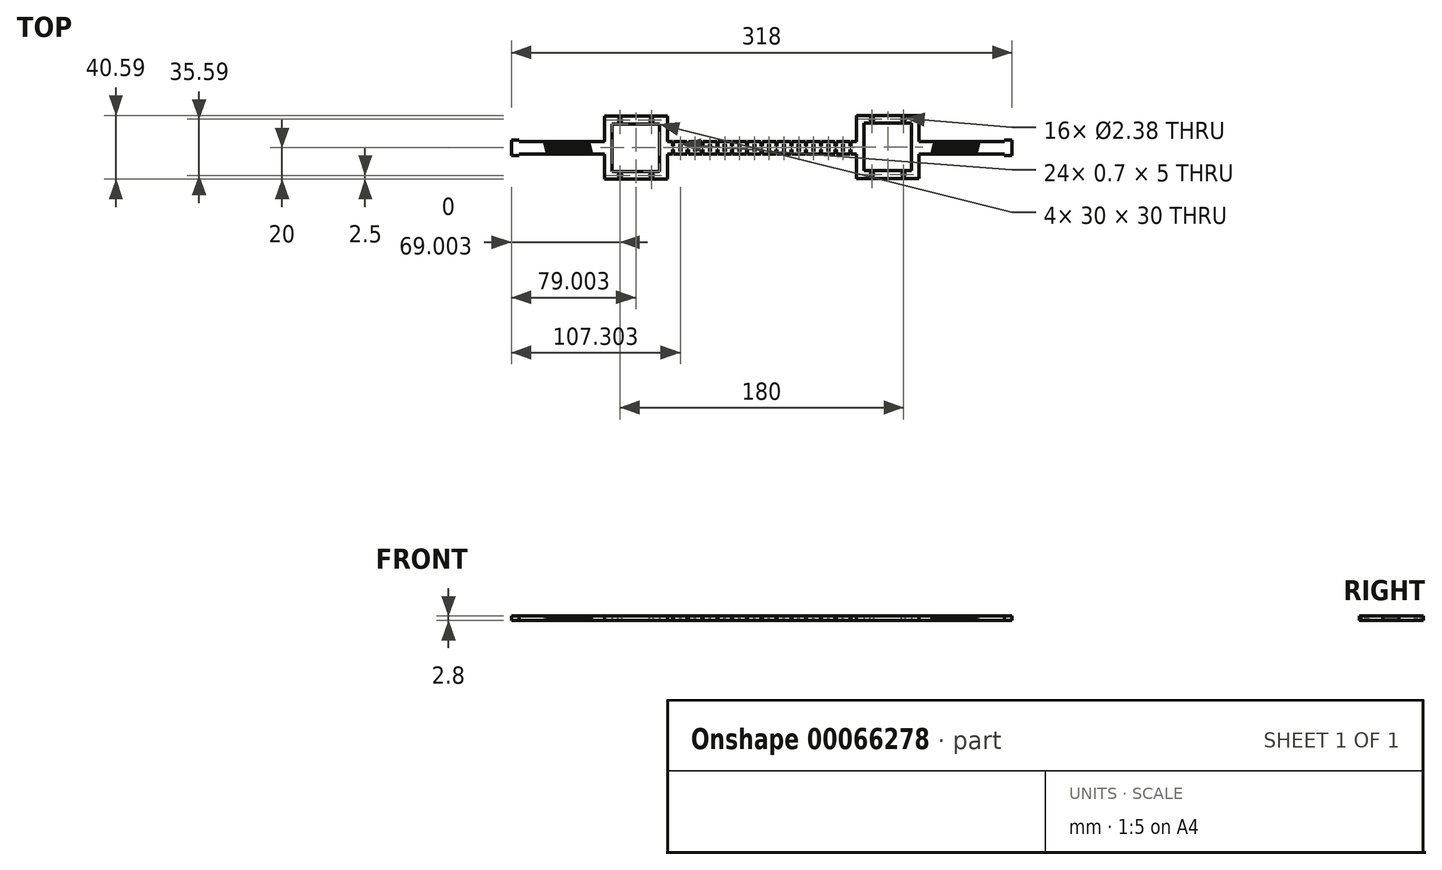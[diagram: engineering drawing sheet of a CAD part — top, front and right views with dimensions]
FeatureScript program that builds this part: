
annotation { "Feature Type Name" : "Feature", "Feature Type Description" : "" }
export const myFeature = defineFeature(function(context is Context, id is Id, definition is map)
    precondition{}
    {
        {
            var Q0;
            Q0=qCreatedBy(makeId("Top.planeOp"),FACE);
            var sketch = newSketch(context, id + "F0", { "sketchPlane" : qUnion([Q0])});
            skLineSegment(sketch, "E0.bottom", {"start": v(-118.62, 8) * mm, "end": v(-64.62, 8) * mm});
            skLineSegment(sketch, "E0.top", {"start": v(-118.62, 0) * mm, "end": v(-64.62, 0) * mm});
            skLineSegment(sketch, "E1.bottom", {"start": v(-64.62, 24) * mm, "end": v(-24.62, 24) * mm});
            skLineSegment(sketch, "E1.top", {"start": v(-64.62, -16) * mm, "end": v(-24.62, -16) * mm});
            skLineSegment(sketch, "E1.left", {"start": v(-64.62, 24) * mm, "end": v(-64.62, 8) * mm});
            skLineSegment(sketch, "E1.right", {"start": v(-24.62, 24) * mm, "end": v(-24.62, 8) * mm});
            skLineSegment(sketch, "E2.0", {"start": v(-59.62, 19) * mm, "end": v(-29.62, 19) * mm});
            skLineSegment(sketch, "E2.1", {"start": v(-59.62, 19) * mm, "end": v(-59.62, -11) * mm});
            skLineSegment(sketch, "E2.2", {"start": v(-59.62, -11) * mm, "end": v(-29.62, -11) * mm});
            skLineSegment(sketch, "E2.3", {"start": v(-29.62, 19) * mm, "end": v(-29.62, -11) * mm});
            skLineSegment(sketch, "E3.bottom", {"start": v(95.38, 24.6) * mm, "end": v(135.38, 24.6) * mm});
            skLineSegment(sketch, "E3.top", {"start": v(95.38, -15.4) * mm, "end": v(135.38, -15.4) * mm});
            skLineSegment(sketch, "E3.left", {"start": v(95.38, 24.6) * mm, "end": v(95.38, 8) * mm});
            skLineSegment(sketch, "E3.right", {"start": v(135.38, 24.6) * mm, "end": v(135.38, 8) * mm});
            skLineSegment(sketch, "E4.0", {"start": v(100.38, 19.6) * mm, "end": v(130.38, 19.6) * mm});
            skLineSegment(sketch, "E4.1", {"start": v(100.38, 19.6) * mm, "end": v(100.38, -10.4) * mm});
            skLineSegment(sketch, "E4.2", {"start": v(100.38, -10.4) * mm, "end": v(130.38, -10.4) * mm});
            skLineSegment(sketch, "E4.3", {"start": v(130.38, 19.6) * mm, "end": v(130.38, -10.4) * mm});
            skLineSegment(sketch, "E5.trimOffspring", {"start": v(-24.62, 8) * mm, "end": v(95.38, 8) * mm});
            skLineSegment(sketch, "E6.trimOffspring", {"start": v(-24.62, 0) * mm, "end": v(95.38, 0) * mm});
            skLineSegment(sketch, "E7.trimOffspring", {"start": v(-24.62, 0) * mm, "end": v(-24.62, -16) * mm});
            skLineSegment(sketch, "E8.trimOffspring", {"start": v(-64.62, 0) * mm, "end": v(-64.62, -16) * mm});
            skLineSegment(sketch, "E9.trimOffspring", {"start": v(135.38, 8) * mm, "end": v(189.38, 8) * mm});
            skLineSegment(sketch, "E10.trimOffspring", {"start": v(135.38, 0) * mm, "end": v(189.38, 0) * mm});
            skLineSegment(sketch, "E11.trimOffspring", {"start": v(95.38, 0) * mm, "end": v(95.38, -15.4) * mm});
            skLineSegment(sketch, "E12.trimOffspring", {"start": v(135.38, 0) * mm, "end": v(135.38, -15.4) * mm});
            skLineSegment(sketch, "E13.bottom", {"start": v(-123.62, 9) * mm, "end": v(-118.62, 9) * mm});
            skLineSegment(sketch, "E13.top", {"start": v(-123.62, -1) * mm, "end": v(-118.62, -1) * mm});
            skLineSegment(sketch, "E13.left", {"start": v(-123.62, 9) * mm, "end": v(-123.62, -1) * mm});
            skLineSegment(sketch, "E13.right", {"start": v(-118.62, 9) * mm, "end": v(-118.62, 8) * mm});
            skLineSegment(sketch, "E14.trimOffspring", {"start": v(-118.62, 0) * mm, "end": v(-118.62, -1) * mm});
            skLineSegment(sketch, "E15.bottom", {"start": v(194.38, -1) * mm, "end": v(189.38, -1) * mm});
            skLineSegment(sketch, "E15.top", {"start": v(194.38, 9) * mm, "end": v(189.38, 9) * mm});
            skLineSegment(sketch, "E15.left", {"start": v(194.38, -1) * mm, "end": v(194.38, 9) * mm});
            skLineSegment(sketch, "E15.right", {"start": v(189.38, -1) * mm, "end": v(189.38, 0) * mm});
            skLineSegment(sketch, "E16.trimOffspring", {"start": v(189.38, 8) * mm, "end": v(189.38, 9) * mm});
            skSolve(sketch);
        }
        {
            var Q0;
            Q0=makeQuery(id+"F0.imprint","IMPRINT",FACE,{"disambiguationData":[TD([[makeQuery(id+"F0.imprint","IMPRINT",EDGE,{"derivedFrom":sQuery(id+"F0.wireOp",EDGE,"E0.bottom")}),-1.0]])]});
            extrude(context, id + "F1", {"entities" : qUnion([Q0]), "depth" : 2.8 * mm});
        }
        {
            var Q0;
            Q0=makeQuery(id+"F1.opExtrude","CAP_FACE",FACE,{"disambiguationData":[OSD([sQuery(id+"F0.wireOp",EDGE,"E0.bottom"),sQuery(id+"F0.wireOp",EDGE,"E0.top"),sQuery(id+"F0.wireOp",EDGE,"E0.left"),sQuery(id+"F0.wireOp",EDGE,"E0.right")])],"isStart":false});
            var sketch = newSketch(context, id + "F2", { "sketchPlane" : qUnion([Q0])});
            skLineSegment(sketch, "E17", {"start": v(-102.62, 8) * mm, "end": v(-100.62, 0) * mm});
            skLineSegment(sketch, "E18", {"start": v(-101.62, 8) * mm, "end": v(-99.62, 0) * mm});
            skLineSegment(sketch, "E19.1.0.0", {"start": v(-99.62, 8) * mm, "end": v(-97.62, 0) * mm});
            skLineSegment(sketch, "E19.1.0.1", {"start": v(-98.62, 8) * mm, "end": v(-96.62, 0) * mm});
            skLineSegment(sketch, "E19.2.0.0", {"start": v(-96.62, 8) * mm, "end": v(-94.62, 0) * mm});
            skLineSegment(sketch, "E19.2.0.1", {"start": v(-95.62, 8) * mm, "end": v(-93.62, 0) * mm});
            skLineSegment(sketch, "E19.3.0.0", {"start": v(-93.62, 8) * mm, "end": v(-91.62, 0) * mm});
            skLineSegment(sketch, "E19.3.0.1", {"start": v(-92.62, 8) * mm, "end": v(-90.62, 0) * mm});
            skLineSegment(sketch, "E19.4.0.0", {"start": v(-90.62, 8) * mm, "end": v(-88.62, 0) * mm});
            skLineSegment(sketch, "E19.4.0.1", {"start": v(-89.62, 8) * mm, "end": v(-87.62, 0) * mm});
            skLineSegment(sketch, "E19.5.0.0", {"start": v(-87.62, 8) * mm, "end": v(-85.62, 0) * mm});
            skLineSegment(sketch, "E19.5.0.1", {"start": v(-86.62, 8) * mm, "end": v(-84.62, 0) * mm});
            skLineSegment(sketch, "E19.6.0.0", {"start": v(-84.62, 8) * mm, "end": v(-82.62, 0) * mm});
            skLineSegment(sketch, "E19.6.0.1", {"start": v(-83.62, 8) * mm, "end": v(-81.62, 0) * mm});
            skLineSegment(sketch, "E19.7.0.0", {"start": v(-81.62, 8) * mm, "end": v(-79.62, 0) * mm});
            skLineSegment(sketch, "E19.7.0.1", {"start": v(-80.62, 8) * mm, "end": v(-78.62, 0) * mm});
            skLineSegment(sketch, "E19.8.0.0", {"start": v(-78.62, 8) * mm, "end": v(-76.62, 0) * mm});
            skLineSegment(sketch, "E19.8.0.1", {"start": v(-77.62, 8) * mm, "end": v(-75.62, 0) * mm});
            skLineSegment(sketch, "E19.9.0.0", {"start": v(-75.62, 8) * mm, "end": v(-73.62, 0) * mm});
            skLineSegment(sketch, "E19.9.0.1", {"start": v(-74.62, 8) * mm, "end": v(-72.62, 0) * mm});
            skLineSegment(sketch, "E19.direction1", {"start": v(-100.62, 0) * mm, "end": v(-97.62, 0) * mm, "construction": true});
            skLineSegment(sketch, "E20", {"start": v(172.38, 8) * mm, "end": v(170.38, 0) * mm});
            skLineSegment(sketch, "E21", {"start": v(171.38, 0) * mm, "end": v(173.38, 8) * mm});
            skLineSegment(sketch, "E22.1.0.0", {"start": v(168.38, 0) * mm, "end": v(170.38, 8) * mm});
            skLineSegment(sketch, "E22.1.0.1", {"start": v(169.38, 8) * mm, "end": v(167.38, 0) * mm});
            skLineSegment(sketch, "E22.2.0.0", {"start": v(165.38, 0) * mm, "end": v(167.38, 8) * mm});
            skLineSegment(sketch, "E22.2.0.1", {"start": v(166.38, 8) * mm, "end": v(164.38, 0) * mm});
            skLineSegment(sketch, "E22.direction1", {"start": v(171.38, 0) * mm, "end": v(168.38, 0) * mm, "construction": true});
            skLineSegment(sketch, "E23.0.3.0", {"start": v(162.38, 0) * mm, "end": v(164.38, 8) * mm});
            skLineSegment(sketch, "E23.3.3.0", {"start": v(163.38, 8) * mm, "end": v(161.38, 0) * mm});
            skLineSegment(sketch, "E23.0.4.0", {"start": v(159.38, 0) * mm, "end": v(161.38, 8) * mm});
            skLineSegment(sketch, "E23.3.4.0", {"start": v(160.38, 8) * mm, "end": v(158.38, 0) * mm});
            skLineSegment(sketch, "E23.0.5.0", {"start": v(156.38, 0) * mm, "end": v(158.38, 8) * mm});
            skLineSegment(sketch, "E23.3.5.0", {"start": v(157.38, 8) * mm, "end": v(155.38, 0) * mm});
            skLineSegment(sketch, "E23.0.6.0", {"start": v(153.38, 0) * mm, "end": v(155.38, 8) * mm});
            skLineSegment(sketch, "E23.3.6.0", {"start": v(154.38, 8) * mm, "end": v(152.38, 0) * mm});
            skLineSegment(sketch, "E23.0.7.0", {"start": v(150.38, 0) * mm, "end": v(152.38, 8) * mm});
            skLineSegment(sketch, "E23.3.7.0", {"start": v(151.38, 8) * mm, "end": v(149.38, 0) * mm});
            skLineSegment(sketch, "E23.0.8.0", {"start": v(147.38, 0) * mm, "end": v(149.38, 8) * mm});
            skLineSegment(sketch, "E23.3.8.0", {"start": v(148.38, 8) * mm, "end": v(146.38, 0) * mm});
            skLineSegment(sketch, "E23.0.9.0", {"start": v(144.38, 0) * mm, "end": v(146.38, 8) * mm});
            skLineSegment(sketch, "E23.3.9.0", {"start": v(145.38, 8) * mm, "end": v(143.38, 0) * mm});
            skCircle(sketch, "E24", {"center": v(105.38, 22.1) * mm, "radius": 1.2 * mm});
            skCircle(sketch, "E25", {"center": v(125.38, 22.1) * mm, "radius": 1.2 * mm});
            skCircle(sketch, "E26", {"center": v(105.38, -12.9) * mm, "radius": 1.2 * mm});
            skCircle(sketch, "E27", {"center": v(125.38, -12.9) * mm, "radius": 1.2 * mm});
            skCircle(sketch, "E28", {"center": v(-54.62, -13.5) * mm, "radius": 1.2 * mm});
            skCircle(sketch, "E29", {"center": v(-34.62, -13.5) * mm, "radius": 1.2 * mm});
            skCircle(sketch, "E30", {"center": v(-54.62, 21.5) * mm, "radius": 1.2 * mm});
            skCircle(sketch, "E31", {"center": v(-34.62, 21.5) * mm, "radius": 1.2 * mm});
            skLineSegment(sketch, "E32.bottom", {"start": v(-21.37, 8) * mm, "end": v(-20.67, 8) * mm});
            skLineSegment(sketch, "E32.top", {"start": v(-21.37, 5) * mm, "end": v(-20.67, 5) * mm});
            skLineSegment(sketch, "E32.left", {"start": v(-21.37, 8) * mm, "end": v(-21.37, 5) * mm});
            skLineSegment(sketch, "E32.right", {"start": v(-20.67, 8) * mm, "end": v(-20.67, 5) * mm});
            skLineSegment(sketch, "E33.bottom", {"start": v(-21.37, 0) * mm, "end": v(-20.67, 0) * mm});
            skLineSegment(sketch, "E33.top", {"start": v(-21.37, 3) * mm, "end": v(-20.67, 3) * mm});
            skLineSegment(sketch, "E33.left", {"start": v(-21.37, 0) * mm, "end": v(-21.37, 3) * mm});
            skLineSegment(sketch, "E33.right", {"start": v(-20.67, 0) * mm, "end": v(-20.67, 3) * mm});
            skLineSegment(sketch, "E34.bottom", {"start": v(-16.67, 6.5) * mm, "end": v(-15.97, 6.5) * mm});
            skLineSegment(sketch, "E34.top", {"start": v(-16.67, 1.5) * mm, "end": v(-15.97, 1.5) * mm});
            skLineSegment(sketch, "E34.left", {"start": v(-16.67, 6.5) * mm, "end": v(-16.67, 1.5) * mm});
            skLineSegment(sketch, "E34.right", {"start": v(-15.97, 6.5) * mm, "end": v(-15.97, 1.5) * mm});
            skLineSegment(sketch, "E35.1.0.0", {"start": v(-11.97, 8) * mm, "end": v(-11.97, 5) * mm});
            skLineSegment(sketch, "E35.1.0.1", {"start": v(-11.97, 8) * mm, "end": v(-11.27, 8) * mm});
            skLineSegment(sketch, "E35.1.0.2", {"start": v(-11.27, 8) * mm, "end": v(-11.27, 5) * mm});
            skLineSegment(sketch, "E35.1.0.3", {"start": v(-11.97, 5) * mm, "end": v(-11.27, 5) * mm});
            skLineSegment(sketch, "E35.1.0.4", {"start": v(-11.97, 3) * mm, "end": v(-11.27, 3) * mm});
            skLineSegment(sketch, "E35.1.0.5", {"start": v(-11.97, 0) * mm, "end": v(-11.97, 3) * mm});
            skLineSegment(sketch, "E35.1.0.6", {"start": v(-11.97, 0) * mm, "end": v(-11.27, 0) * mm});
            skLineSegment(sketch, "E35.1.0.7", {"start": v(-11.27, 0) * mm, "end": v(-11.27, 3) * mm});
            skLineSegment(sketch, "E35.1.0.8", {"start": v(-7.27, 6.5) * mm, "end": v(-7.27, 1.5) * mm});
            skLineSegment(sketch, "E35.1.0.9", {"start": v(-7.27, 6.5) * mm, "end": v(-6.57, 6.5) * mm});
            skLineSegment(sketch, "E35.1.0.10", {"start": v(-6.57, 6.5) * mm, "end": v(-6.57, 1.5) * mm});
            skLineSegment(sketch, "E35.1.0.11", {"start": v(-7.27, 1.5) * mm, "end": v(-6.57, 1.5) * mm});
            skLineSegment(sketch, "E35.2.0.0", {"start": v(-2.57, 8) * mm, "end": v(-2.57, 5) * mm});
            skLineSegment(sketch, "E35.2.0.1", {"start": v(-2.57, 8) * mm, "end": v(-1.87, 8) * mm});
            skLineSegment(sketch, "E35.2.0.2", {"start": v(-1.87, 8) * mm, "end": v(-1.87, 5) * mm});
            skLineSegment(sketch, "E35.2.0.3", {"start": v(-2.57, 5) * mm, "end": v(-1.87, 5) * mm});
            skLineSegment(sketch, "E35.2.0.4", {"start": v(-2.57, 3) * mm, "end": v(-1.87, 3) * mm});
            skLineSegment(sketch, "E35.2.0.5", {"start": v(-2.57, 0) * mm, "end": v(-2.57, 3) * mm});
            skLineSegment(sketch, "E35.2.0.6", {"start": v(-2.57, 0) * mm, "end": v(-1.87, 0) * mm});
            skLineSegment(sketch, "E35.2.0.7", {"start": v(-1.87, 0) * mm, "end": v(-1.87, 3) * mm});
            skLineSegment(sketch, "E35.2.0.8", {"start": v(2.13, 6.5) * mm, "end": v(2.13, 1.5) * mm});
            skLineSegment(sketch, "E35.2.0.9", {"start": v(2.13, 6.5) * mm, "end": v(2.83, 6.5) * mm});
            skLineSegment(sketch, "E35.2.0.10", {"start": v(2.83, 6.5) * mm, "end": v(2.83, 1.5) * mm});
            skLineSegment(sketch, "E35.2.0.11", {"start": v(2.13, 1.5) * mm, "end": v(2.83, 1.5) * mm});
            skLineSegment(sketch, "E35.3.0.0", {"start": v(6.83, 8) * mm, "end": v(6.83, 5) * mm});
            skLineSegment(sketch, "E35.3.0.1", {"start": v(6.83, 8) * mm, "end": v(7.53, 8) * mm});
            skLineSegment(sketch, "E35.3.0.2", {"start": v(7.53, 8) * mm, "end": v(7.53, 5) * mm});
            skLineSegment(sketch, "E35.3.0.3", {"start": v(6.83, 5) * mm, "end": v(7.53, 5) * mm});
            skLineSegment(sketch, "E35.3.0.4", {"start": v(6.83, 3) * mm, "end": v(7.53, 3) * mm});
            skLineSegment(sketch, "E35.3.0.5", {"start": v(6.83, 0) * mm, "end": v(6.83, 3) * mm});
            skLineSegment(sketch, "E35.3.0.6", {"start": v(6.83, 0) * mm, "end": v(7.53, 0) * mm});
            skLineSegment(sketch, "E35.3.0.7", {"start": v(7.53, 0) * mm, "end": v(7.53, 3) * mm});
            skLineSegment(sketch, "E35.3.0.8", {"start": v(11.53, 6.5) * mm, "end": v(11.53, 1.5) * mm});
            skLineSegment(sketch, "E35.3.0.9", {"start": v(11.53, 6.5) * mm, "end": v(12.23, 6.5) * mm});
            skLineSegment(sketch, "E35.3.0.10", {"start": v(12.23, 6.5) * mm, "end": v(12.23, 1.5) * mm});
            skLineSegment(sketch, "E35.3.0.11", {"start": v(11.53, 1.5) * mm, "end": v(12.23, 1.5) * mm});
            skLineSegment(sketch, "E35.4.0.0", {"start": v(16.23, 8) * mm, "end": v(16.23, 5) * mm});
            skLineSegment(sketch, "E35.4.0.1", {"start": v(16.23, 8) * mm, "end": v(16.93, 8) * mm});
            skLineSegment(sketch, "E35.4.0.2", {"start": v(16.93, 8) * mm, "end": v(16.93, 5) * mm});
            skLineSegment(sketch, "E35.4.0.3", {"start": v(16.23, 5) * mm, "end": v(16.93, 5) * mm});
            skLineSegment(sketch, "E35.4.0.4", {"start": v(16.23, 3) * mm, "end": v(16.93, 3) * mm});
            skLineSegment(sketch, "E35.4.0.5", {"start": v(16.23, 0) * mm, "end": v(16.23, 3) * mm});
            skLineSegment(sketch, "E35.4.0.6", {"start": v(16.23, 0) * mm, "end": v(16.93, 0) * mm});
            skLineSegment(sketch, "E35.4.0.7", {"start": v(16.93, 0) * mm, "end": v(16.93, 3) * mm});
            skLineSegment(sketch, "E35.4.0.8", {"start": v(20.93, 6.5) * mm, "end": v(20.93, 1.5) * mm});
            skLineSegment(sketch, "E35.4.0.9", {"start": v(20.93, 6.5) * mm, "end": v(21.63, 6.5) * mm});
            skLineSegment(sketch, "E35.4.0.10", {"start": v(21.63, 6.5) * mm, "end": v(21.63, 1.5) * mm});
            skLineSegment(sketch, "E35.4.0.11", {"start": v(20.93, 1.5) * mm, "end": v(21.63, 1.5) * mm});
            skLineSegment(sketch, "E35.5.0.0", {"start": v(25.63, 8) * mm, "end": v(25.63, 5) * mm});
            skLineSegment(sketch, "E35.5.0.1", {"start": v(25.63, 8) * mm, "end": v(26.33, 8) * mm});
            skLineSegment(sketch, "E35.5.0.2", {"start": v(26.33, 8) * mm, "end": v(26.33, 5) * mm});
            skLineSegment(sketch, "E35.5.0.3", {"start": v(25.63, 5) * mm, "end": v(26.33, 5) * mm});
            skLineSegment(sketch, "E35.5.0.4", {"start": v(25.63, 3) * mm, "end": v(26.33, 3) * mm});
            skLineSegment(sketch, "E35.5.0.5", {"start": v(25.63, 0) * mm, "end": v(25.63, 3) * mm});
            skLineSegment(sketch, "E35.5.0.6", {"start": v(25.63, 0) * mm, "end": v(26.33, 0) * mm});
            skLineSegment(sketch, "E35.5.0.7", {"start": v(26.33, 0) * mm, "end": v(26.33, 3) * mm});
            skLineSegment(sketch, "E35.5.0.8", {"start": v(30.33, 6.5) * mm, "end": v(30.33, 1.5) * mm});
            skLineSegment(sketch, "E35.5.0.9", {"start": v(30.33, 6.5) * mm, "end": v(31.03, 6.5) * mm});
            skLineSegment(sketch, "E35.5.0.10", {"start": v(31.03, 6.5) * mm, "end": v(31.03, 1.5) * mm});
            skLineSegment(sketch, "E35.5.0.11", {"start": v(30.33, 1.5) * mm, "end": v(31.03, 1.5) * mm});
            skLineSegment(sketch, "E35.6.0.0", {"start": v(35.03, 8) * mm, "end": v(35.03, 5) * mm});
            skLineSegment(sketch, "E35.6.0.1", {"start": v(35.03, 8) * mm, "end": v(35.73, 8) * mm});
            skLineSegment(sketch, "E35.6.0.2", {"start": v(35.73, 8) * mm, "end": v(35.73, 5) * mm});
            skLineSegment(sketch, "E35.6.0.3", {"start": v(35.03, 5) * mm, "end": v(35.73, 5) * mm});
            skLineSegment(sketch, "E35.6.0.4", {"start": v(35.03, 3) * mm, "end": v(35.73, 3) * mm});
            skLineSegment(sketch, "E35.6.0.5", {"start": v(35.03, 0) * mm, "end": v(35.03, 3) * mm});
            skLineSegment(sketch, "E35.6.0.6", {"start": v(35.03, 0) * mm, "end": v(35.73, 0) * mm});
            skLineSegment(sketch, "E35.6.0.7", {"start": v(35.73, 0) * mm, "end": v(35.73, 3) * mm});
            skLineSegment(sketch, "E35.6.0.8", {"start": v(39.73, 6.5) * mm, "end": v(39.73, 1.5) * mm});
            skLineSegment(sketch, "E35.6.0.9", {"start": v(39.73, 6.5) * mm, "end": v(40.43, 6.5) * mm});
            skLineSegment(sketch, "E35.6.0.10", {"start": v(40.43, 6.5) * mm, "end": v(40.43, 1.5) * mm});
            skLineSegment(sketch, "E35.6.0.11", {"start": v(39.73, 1.5) * mm, "end": v(40.43, 1.5) * mm});
            skLineSegment(sketch, "E35.7.0.0", {"start": v(44.43, 8) * mm, "end": v(44.43, 5) * mm});
            skLineSegment(sketch, "E35.7.0.1", {"start": v(44.43, 8) * mm, "end": v(45.13, 8) * mm});
            skLineSegment(sketch, "E35.7.0.2", {"start": v(45.13, 8) * mm, "end": v(45.13, 5) * mm});
            skLineSegment(sketch, "E35.7.0.3", {"start": v(44.43, 5) * mm, "end": v(45.13, 5) * mm});
            skLineSegment(sketch, "E35.7.0.4", {"start": v(44.43, 3) * mm, "end": v(45.13, 3) * mm});
            skLineSegment(sketch, "E35.7.0.5", {"start": v(44.43, 0) * mm, "end": v(44.43, 3) * mm});
            skLineSegment(sketch, "E35.7.0.6", {"start": v(44.43, 0) * mm, "end": v(45.13, 0) * mm});
            skLineSegment(sketch, "E35.7.0.7", {"start": v(45.13, 0) * mm, "end": v(45.13, 3) * mm});
            skLineSegment(sketch, "E35.7.0.8", {"start": v(49.13, 6.5) * mm, "end": v(49.13, 1.5) * mm});
            skLineSegment(sketch, "E35.7.0.9", {"start": v(49.13, 6.5) * mm, "end": v(49.83, 6.5) * mm});
            skLineSegment(sketch, "E35.7.0.10", {"start": v(49.83, 6.5) * mm, "end": v(49.83, 1.5) * mm});
            skLineSegment(sketch, "E35.7.0.11", {"start": v(49.13, 1.5) * mm, "end": v(49.83, 1.5) * mm});
            skLineSegment(sketch, "E35.8.0.0", {"start": v(53.83, 8) * mm, "end": v(53.83, 5) * mm});
            skLineSegment(sketch, "E35.8.0.1", {"start": v(53.83, 8) * mm, "end": v(54.53, 8) * mm});
            skLineSegment(sketch, "E35.8.0.2", {"start": v(54.53, 8) * mm, "end": v(54.53, 5) * mm});
            skLineSegment(sketch, "E35.8.0.3", {"start": v(53.83, 5) * mm, "end": v(54.53, 5) * mm});
            skLineSegment(sketch, "E35.8.0.4", {"start": v(53.83, 3) * mm, "end": v(54.53, 3) * mm});
            skLineSegment(sketch, "E35.8.0.5", {"start": v(53.83, 0) * mm, "end": v(53.83, 3) * mm});
            skLineSegment(sketch, "E35.8.0.6", {"start": v(53.83, 0) * mm, "end": v(54.53, 0) * mm});
            skLineSegment(sketch, "E35.8.0.7", {"start": v(54.53, 0) * mm, "end": v(54.53, 3) * mm});
            skLineSegment(sketch, "E35.8.0.8", {"start": v(58.53, 6.5) * mm, "end": v(58.53, 1.5) * mm});
            skLineSegment(sketch, "E35.8.0.9", {"start": v(58.53, 6.5) * mm, "end": v(59.23, 6.5) * mm});
            skLineSegment(sketch, "E35.8.0.10", {"start": v(59.23, 6.5) * mm, "end": v(59.23, 1.5) * mm});
            skLineSegment(sketch, "E35.8.0.11", {"start": v(58.53, 1.5) * mm, "end": v(59.23, 1.5) * mm});
            skLineSegment(sketch, "E35.9.0.0", {"start": v(63.23, 8) * mm, "end": v(63.23, 5) * mm});
            skLineSegment(sketch, "E35.9.0.1", {"start": v(63.23, 8) * mm, "end": v(63.93, 8) * mm});
            skLineSegment(sketch, "E35.9.0.2", {"start": v(63.93, 8) * mm, "end": v(63.93, 5) * mm});
            skLineSegment(sketch, "E35.9.0.3", {"start": v(63.23, 5) * mm, "end": v(63.93, 5) * mm});
            skLineSegment(sketch, "E35.9.0.4", {"start": v(63.23, 3) * mm, "end": v(63.93, 3) * mm});
            skLineSegment(sketch, "E35.9.0.5", {"start": v(63.23, 0) * mm, "end": v(63.23, 3) * mm});
            skLineSegment(sketch, "E35.9.0.6", {"start": v(63.23, 0) * mm, "end": v(63.93, 0) * mm});
            skLineSegment(sketch, "E35.9.0.7", {"start": v(63.93, 0) * mm, "end": v(63.93, 3) * mm});
            skLineSegment(sketch, "E35.9.0.8", {"start": v(67.93, 6.5) * mm, "end": v(67.93, 1.5) * mm});
            skLineSegment(sketch, "E35.9.0.9", {"start": v(67.93, 6.5) * mm, "end": v(68.63, 6.5) * mm});
            skLineSegment(sketch, "E35.9.0.10", {"start": v(68.63, 6.5) * mm, "end": v(68.63, 1.5) * mm});
            skLineSegment(sketch, "E35.9.0.11", {"start": v(67.93, 1.5) * mm, "end": v(68.63, 1.5) * mm});
            skLineSegment(sketch, "E35.direction1", {"start": v(-21.37, 5) * mm, "end": v(-11.97, 5) * mm, "construction": true});
            skLineSegment(sketch, "E36.0.10.0", {"start": v(72.63, 8) * mm, "end": v(72.63, 5) * mm});
            skLineSegment(sketch, "E36.3.10.0", {"start": v(72.63, 8) * mm, "end": v(73.33, 8) * mm});
            skLineSegment(sketch, "E36.6.10.0", {"start": v(73.33, 8) * mm, "end": v(73.33, 5) * mm});
            skLineSegment(sketch, "E36.9.10.0", {"start": v(72.63, 5) * mm, "end": v(73.33, 5) * mm});
            skLineSegment(sketch, "E36.12.10.0", {"start": v(72.63, 3) * mm, "end": v(73.33, 3) * mm});
            skLineSegment(sketch, "E36.15.10.0", {"start": v(72.63, 0) * mm, "end": v(72.63, 3) * mm});
            skLineSegment(sketch, "E36.18.10.0", {"start": v(72.63, 0) * mm, "end": v(73.33, 0) * mm});
            skLineSegment(sketch, "E36.21.10.0", {"start": v(73.33, 0) * mm, "end": v(73.33, 3) * mm});
            skLineSegment(sketch, "E36.24.10.0", {"start": v(77.33, 6.5) * mm, "end": v(77.33, 1.5) * mm});
            skLineSegment(sketch, "E36.27.10.0", {"start": v(77.33, 6.5) * mm, "end": v(78.03, 6.5) * mm});
            skLineSegment(sketch, "E36.30.10.0", {"start": v(78.03, 6.5) * mm, "end": v(78.03, 1.5) * mm});
            skLineSegment(sketch, "E36.33.10.0", {"start": v(77.33, 1.5) * mm, "end": v(78.03, 1.5) * mm});
            skLineSegment(sketch, "E36.0.11.0", {"start": v(82.03, 8) * mm, "end": v(82.03, 5) * mm});
            skLineSegment(sketch, "E36.3.11.0", {"start": v(82.03, 8) * mm, "end": v(82.73, 8) * mm});
            skLineSegment(sketch, "E36.6.11.0", {"start": v(82.73, 8) * mm, "end": v(82.73, 5) * mm});
            skLineSegment(sketch, "E36.9.11.0", {"start": v(82.03, 5) * mm, "end": v(82.73, 5) * mm});
            skLineSegment(sketch, "E36.12.11.0", {"start": v(82.03, 3) * mm, "end": v(82.73, 3) * mm});
            skLineSegment(sketch, "E36.15.11.0", {"start": v(82.03, 0) * mm, "end": v(82.03, 3) * mm});
            skLineSegment(sketch, "E36.18.11.0", {"start": v(82.03, 0) * mm, "end": v(82.73, 0) * mm});
            skLineSegment(sketch, "E36.21.11.0", {"start": v(82.73, 0) * mm, "end": v(82.73, 3) * mm});
            skLineSegment(sketch, "E36.24.11.0", {"start": v(86.73, 6.5) * mm, "end": v(86.73, 1.5) * mm});
            skLineSegment(sketch, "E36.27.11.0", {"start": v(86.73, 6.5) * mm, "end": v(87.43, 6.5) * mm});
            skLineSegment(sketch, "E36.30.11.0", {"start": v(87.43, 6.5) * mm, "end": v(87.43, 1.5) * mm});
            skLineSegment(sketch, "E36.33.11.0", {"start": v(86.73, 1.5) * mm, "end": v(87.43, 1.5) * mm});
            skLineSegment(sketch, "E37.bottom", {"start": v(91.43, 8) * mm, "end": v(92.13, 8) * mm});
            skLineSegment(sketch, "E37.left", {"start": v(91.43, 8) * mm, "end": v(91.43, 5) * mm});
            skLineSegment(sketch, "E37.right", {"start": v(92.13, 8) * mm, "end": v(92.13, 5) * mm});
            skLineSegment(sketch, "E37.top", {"start": v(91.43, 5) * mm, "end": v(92.13, 5) * mm});
            skLineSegment(sketch, "E38.top", {"start": v(91.43, 3) * mm, "end": v(92.13, 3) * mm});
            skLineSegment(sketch, "E38.left", {"start": v(91.43, 0) * mm, "end": v(91.43, 3) * mm});
            skLineSegment(sketch, "E38.right", {"start": v(92.13, 0) * mm, "end": v(92.13, 3) * mm});
            skLineSegment(sketch, "E38.bottom", {"start": v(91.43, 0) * mm, "end": v(92.13, 0) * mm});
            skSolve(sketch);
        }
        {
            var Q0;
            Q0=makeQuery(id+"F2.imprint","IMPRINT",FACE,{"disambiguationData":[TD([[makeQuery(id+"F2.imprint","IMPRINT",EDGE,{"derivedFrom":sQuery(id+"F2.wireOp",EDGE,"E28")}),1.0]])]});
            var Q1;
            Q1=makeQuery(id+"F2.imprint","IMPRINT",FACE,{"disambiguationData":[TD([[makeQuery(id+"F2.imprint","IMPRINT",EDGE,{"derivedFrom":sQuery(id+"F2.wireOp",EDGE,"E29")}),1.0]])]});
            var Q2;
            Q2=makeQuery(id+"F2.imprint","IMPRINT",FACE,{"disambiguationData":[TD([[makeQuery(id+"F2.imprint","IMPRINT",EDGE,{"derivedFrom":sQuery(id+"F2.wireOp",EDGE,"E30")}),1.0]])]});
            var Q3;
            Q3=makeQuery(id+"F2.imprint","IMPRINT",FACE,{"disambiguationData":[TD([[makeQuery(id+"F2.imprint","IMPRINT",EDGE,{"derivedFrom":sQuery(id+"F2.wireOp",EDGE,"E31")}),1.0]])]});
            var Q4;
            Q4=makeQuery(id+"F2.imprint","IMPRINT",FACE,{"disambiguationData":[TD([[makeQuery(id+"F2.imprint","IMPRINT",EDGE,{"derivedFrom":sQuery(id+"F2.wireOp",EDGE,"E24")}),1.0]])]});
            var Q5;
            Q5=makeQuery(id+"F2.imprint","IMPRINT",FACE,{"disambiguationData":[TD([[makeQuery(id+"F2.imprint","IMPRINT",EDGE,{"derivedFrom":sQuery(id+"F2.wireOp",EDGE,"E25")}),1.0]])]});
            var Q6;
            Q6=makeQuery(id+"F2.imprint","IMPRINT",FACE,{"disambiguationData":[TD([[makeQuery(id+"F2.imprint","IMPRINT",EDGE,{"derivedFrom":sQuery(id+"F2.wireOp",EDGE,"E27")}),1.0]])]});
            var Q7;
            Q7=makeQuery(id+"F2.imprint","IMPRINT",FACE,{"disambiguationData":[TD([[makeQuery(id+"F2.imprint","IMPRINT",EDGE,{"derivedFrom":sQuery(id+"F2.wireOp",EDGE,"E26")}),1.0]])]});
            extrude(context, id + "F3", {"entities" : qUnion([Q0, Q1, Q2, Q3, Q4, Q5, Q6, Q7]), "operationType" : NewBodyOperationType.REMOVE, "endBound" : BoundingType.THROUGH_ALL, "oppositeDirection" : true, "depth" : 25 * mm});
        }
        {
            var Q0;
            {var subQ0=sQuery(id+"F2.wireOp",EDGE,"E19.1.0.0");Q0=makeQuery(id+"F2.imprint","IMPRINT",FACE,{"disambiguationData":[TD([[makeQuery(id+"F2.imprint","IMPRINT",EDGE,{"derivedFrom":subQ0}),1.0]])]});}
            var Q1;
            {var subQ0=sQuery(id+"F2.wireOp",EDGE,"E17");Q1=makeQuery(id+"F2.imprint","IMPRINT",FACE,{"disambiguationData":[TD([[makeQuery(id+"F2.imprint","IMPRINT",EDGE,{"derivedFrom":subQ0}),1.0]])]});}
            var Q2;
            {var subQ0=sQuery(id+"F2.wireOp",EDGE,"E19.2.0.0");Q2=makeQuery(id+"F2.imprint","IMPRINT",FACE,{"disambiguationData":[TD([[makeQuery(id+"F2.imprint","IMPRINT",EDGE,{"derivedFrom":subQ0}),1.0]])]});}
            var Q3;
            {var subQ0=sQuery(id+"F2.wireOp",EDGE,"E19.3.0.0");Q3=makeQuery(id+"F2.imprint","IMPRINT",FACE,{"disambiguationData":[TD([[makeQuery(id+"F2.imprint","IMPRINT",EDGE,{"derivedFrom":subQ0}),1.0]])]});}
            var Q4;
            {var subQ0=sQuery(id+"F2.wireOp",EDGE,"E19.4.0.0");Q4=makeQuery(id+"F2.imprint","IMPRINT",FACE,{"disambiguationData":[TD([[makeQuery(id+"F2.imprint","IMPRINT",EDGE,{"derivedFrom":subQ0}),1.0]])]});}
            var Q5;
            {var subQ0=sQuery(id+"F2.wireOp",EDGE,"E19.5.0.0");Q5=makeQuery(id+"F2.imprint","IMPRINT",FACE,{"disambiguationData":[TD([[makeQuery(id+"F2.imprint","IMPRINT",EDGE,{"derivedFrom":subQ0}),1.0]])]});}
            var Q6;
            {var subQ0=sQuery(id+"F2.wireOp",EDGE,"E19.6.0.0");Q6=makeQuery(id+"F2.imprint","IMPRINT",FACE,{"disambiguationData":[TD([[makeQuery(id+"F2.imprint","IMPRINT",EDGE,{"derivedFrom":subQ0}),1.0]])]});}
            var Q7;
            {var subQ0=sQuery(id+"F2.wireOp",EDGE,"E19.7.0.0");Q7=makeQuery(id+"F2.imprint","IMPRINT",FACE,{"disambiguationData":[TD([[makeQuery(id+"F2.imprint","IMPRINT",EDGE,{"derivedFrom":subQ0}),1.0]])]});}
            var Q8;
            {var subQ0=sQuery(id+"F2.wireOp",EDGE,"E19.8.0.0");Q8=makeQuery(id+"F2.imprint","IMPRINT",FACE,{"disambiguationData":[TD([[makeQuery(id+"F2.imprint","IMPRINT",EDGE,{"derivedFrom":subQ0}),1.0]])]});}
            var Q9;
            {var subQ0=sQuery(id+"F2.wireOp",EDGE,"E19.9.0.0");Q9=makeQuery(id+"F2.imprint","IMPRINT",FACE,{"disambiguationData":[TD([[makeQuery(id+"F2.imprint","IMPRINT",EDGE,{"derivedFrom":subQ0}),1.0]])]});}
            var Q10;
            {var subQ0=sQuery(id+"F2.wireOp",EDGE,"E23.0.9.0");Q10=makeQuery(id+"F2.imprint","IMPRINT",FACE,{"disambiguationData":[TD([[makeQuery(id+"F2.imprint","IMPRINT",EDGE,{"derivedFrom":subQ0}),1.0]])]});}
            var Q11;
            {var subQ0=sQuery(id+"F2.wireOp",EDGE,"E23.0.8.0");Q11=makeQuery(id+"F2.imprint","IMPRINT",FACE,{"disambiguationData":[TD([[makeQuery(id+"F2.imprint","IMPRINT",EDGE,{"derivedFrom":subQ0}),1.0]])]});}
            var Q12;
            {var subQ0=sQuery(id+"F2.wireOp",EDGE,"E23.0.7.0");Q12=makeQuery(id+"F2.imprint","IMPRINT",FACE,{"disambiguationData":[TD([[makeQuery(id+"F2.imprint","IMPRINT",EDGE,{"derivedFrom":subQ0}),1.0]])]});}
            var Q13;
            {var subQ0=sQuery(id+"F2.wireOp",EDGE,"E23.0.6.0");Q13=makeQuery(id+"F2.imprint","IMPRINT",FACE,{"disambiguationData":[TD([[makeQuery(id+"F2.imprint","IMPRINT",EDGE,{"derivedFrom":subQ0}),1.0]])]});}
            var Q14;
            {var subQ0=sQuery(id+"F2.wireOp",EDGE,"E23.0.5.0");Q14=makeQuery(id+"F2.imprint","IMPRINT",FACE,{"disambiguationData":[TD([[makeQuery(id+"F2.imprint","IMPRINT",EDGE,{"derivedFrom":subQ0}),1.0]])]});}
            var Q15;
            {var subQ0=sQuery(id+"F2.wireOp",EDGE,"E23.0.4.0");Q15=makeQuery(id+"F2.imprint","IMPRINT",FACE,{"disambiguationData":[TD([[makeQuery(id+"F2.imprint","IMPRINT",EDGE,{"derivedFrom":subQ0}),1.0]])]});}
            var Q16;
            {var subQ0=sQuery(id+"F2.wireOp",EDGE,"E23.0.3.0");Q16=makeQuery(id+"F2.imprint","IMPRINT",FACE,{"disambiguationData":[TD([[makeQuery(id+"F2.imprint","IMPRINT",EDGE,{"derivedFrom":subQ0}),1.0]])]});}
            var Q17;
            {var subQ0=sQuery(id+"F2.wireOp",EDGE,"E22.2.0.0");Q17=makeQuery(id+"F2.imprint","IMPRINT",FACE,{"disambiguationData":[TD([[makeQuery(id+"F2.imprint","IMPRINT",EDGE,{"derivedFrom":subQ0}),1.0]])]});}
            var Q18;
            {var subQ0=sQuery(id+"F2.wireOp",EDGE,"E22.1.0.0");Q18=makeQuery(id+"F2.imprint","IMPRINT",FACE,{"disambiguationData":[TD([[makeQuery(id+"F2.imprint","IMPRINT",EDGE,{"derivedFrom":subQ0}),1.0]])]});}
            var Q19;
            {var subQ0=sQuery(id+"F2.wireOp",EDGE,"E20");Q19=makeQuery(id+"F2.imprint","IMPRINT",FACE,{"disambiguationData":[TD([[makeQuery(id+"F2.imprint","IMPRINT",EDGE,{"derivedFrom":subQ0}),1.0]])]});}
            extrude(context, id + "F4", {"entities" : qUnion([Q0, Q1, Q2, Q3, Q4, Q5, Q6, Q7, Q8, Q9, Q10, Q11, Q12, Q13, Q14, Q15, Q16, Q17, Q18, Q19]), "operationType" : NewBodyOperationType.REMOVE, "oppositeDirection" : true, "depth" : 1.5 * mm});
        }
        {
            var Q0;
            Q0=makeQuery(id+"F2.imprint","IMPRINT",FACE,{"disambiguationData":[TD([[makeQuery(id+"F2.imprint","IMPRINT",EDGE,{"derivedFrom":sQuery(id+"F2.wireOp",EDGE,"E32.bottom")}),-1.0]])]});
            var Q1;
            Q1=makeQuery(id+"F2.imprint","IMPRINT",FACE,{"disambiguationData":[TD([[makeQuery(id+"F2.imprint","IMPRINT",EDGE,{"derivedFrom":sQuery(id+"F2.wireOp",EDGE,"E33.bottom")}),1.0]])]});
            var Q2;
            Q2=makeQuery(id+"F2.imprint","IMPRINT",FACE,{"disambiguationData":[TD([[makeQuery(id+"F2.imprint","IMPRINT",EDGE,{"derivedFrom":sQuery(id+"F2.wireOp",EDGE,"E34.bottom")}),-1.0]])]});
            var Q3;
            Q3=makeQuery(id+"F2.imprint","IMPRINT",FACE,{"disambiguationData":[TD([[makeQuery(id+"F2.imprint","IMPRINT",EDGE,{"derivedFrom":sQuery(id+"F2.wireOp",EDGE,"E35.1.0.0")}),1.0]])]});
            var Q4;
            Q4=makeQuery(id+"F2.imprint","IMPRINT",FACE,{"disambiguationData":[TD([[makeQuery(id+"F2.imprint","IMPRINT",EDGE,{"derivedFrom":sQuery(id+"F2.wireOp",EDGE,"E35.1.0.4")}),-1.0]])]});
            var Q5;
            Q5=makeQuery(id+"F2.imprint","IMPRINT",FACE,{"disambiguationData":[TD([[makeQuery(id+"F2.imprint","IMPRINT",EDGE,{"derivedFrom":sQuery(id+"F2.wireOp",EDGE,"E35.1.0.8")}),1.0]])]});
            var Q6;
            Q6=makeQuery(id+"F2.imprint","IMPRINT",FACE,{"disambiguationData":[TD([[makeQuery(id+"F2.imprint","IMPRINT",EDGE,{"derivedFrom":sQuery(id+"F2.wireOp",EDGE,"E35.2.0.4")}),-1.0]])]});
            var Q7;
            Q7=makeQuery(id+"F2.imprint","IMPRINT",FACE,{"disambiguationData":[TD([[makeQuery(id+"F2.imprint","IMPRINT",EDGE,{"derivedFrom":sQuery(id+"F2.wireOp",EDGE,"E35.2.0.0")}),1.0]])]});
            var Q8;
            Q8=makeQuery(id+"F2.imprint","IMPRINT",FACE,{"disambiguationData":[TD([[makeQuery(id+"F2.imprint","IMPRINT",EDGE,{"derivedFrom":sQuery(id+"F2.wireOp",EDGE,"E35.2.0.8")}),1.0]])]});
            var Q9;
            Q9=makeQuery(id+"F2.imprint","IMPRINT",FACE,{"disambiguationData":[TD([[makeQuery(id+"F2.imprint","IMPRINT",EDGE,{"derivedFrom":sQuery(id+"F2.wireOp",EDGE,"E35.3.0.0")}),1.0]])]});
            var Q10;
            Q10=makeQuery(id+"F2.imprint","IMPRINT",FACE,{"disambiguationData":[TD([[makeQuery(id+"F2.imprint","IMPRINT",EDGE,{"derivedFrom":sQuery(id+"F2.wireOp",EDGE,"E35.3.0.4")}),-1.0]])]});
            var Q11;
            Q11=makeQuery(id+"F2.imprint","IMPRINT",FACE,{"disambiguationData":[TD([[makeQuery(id+"F2.imprint","IMPRINT",EDGE,{"derivedFrom":sQuery(id+"F2.wireOp",EDGE,"E35.3.0.8")}),1.0]])]});
            var Q12;
            Q12=makeQuery(id+"F2.imprint","IMPRINT",FACE,{"disambiguationData":[TD([[makeQuery(id+"F2.imprint","IMPRINT",EDGE,{"derivedFrom":sQuery(id+"F2.wireOp",EDGE,"E35.4.0.0")}),1.0]])]});
            var Q13;
            Q13=makeQuery(id+"F2.imprint","IMPRINT",FACE,{"disambiguationData":[TD([[makeQuery(id+"F2.imprint","IMPRINT",EDGE,{"derivedFrom":sQuery(id+"F2.wireOp",EDGE,"E35.4.0.4")}),-1.0]])]});
            var Q14;
            Q14=makeQuery(id+"F2.imprint","IMPRINT",FACE,{"disambiguationData":[TD([[makeQuery(id+"F2.imprint","IMPRINT",EDGE,{"derivedFrom":sQuery(id+"F2.wireOp",EDGE,"E35.4.0.8")}),1.0]])]});
            var Q15;
            Q15=makeQuery(id+"F2.imprint","IMPRINT",FACE,{"disambiguationData":[TD([[makeQuery(id+"F2.imprint","IMPRINT",EDGE,{"derivedFrom":sQuery(id+"F2.wireOp",EDGE,"E35.5.0.0")}),1.0]])]});
            var Q16;
            Q16=makeQuery(id+"F2.imprint","IMPRINT",FACE,{"disambiguationData":[TD([[makeQuery(id+"F2.imprint","IMPRINT",EDGE,{"derivedFrom":sQuery(id+"F2.wireOp",EDGE,"E35.5.0.4")}),-1.0]])]});
            var Q17;
            Q17=makeQuery(id+"F2.imprint","IMPRINT",FACE,{"disambiguationData":[TD([[makeQuery(id+"F2.imprint","IMPRINT",EDGE,{"derivedFrom":sQuery(id+"F2.wireOp",EDGE,"E35.5.0.8")}),1.0]])]});
            var Q18;
            Q18=makeQuery(id+"F2.imprint","IMPRINT",FACE,{"disambiguationData":[TD([[makeQuery(id+"F2.imprint","IMPRINT",EDGE,{"derivedFrom":sQuery(id+"F2.wireOp",EDGE,"E35.6.0.4")}),-1.0]])]});
            var Q19;
            Q19=makeQuery(id+"F2.imprint","IMPRINT",FACE,{"disambiguationData":[TD([[makeQuery(id+"F2.imprint","IMPRINT",EDGE,{"derivedFrom":sQuery(id+"F2.wireOp",EDGE,"E35.6.0.0")}),1.0]])]});
            var Q20;
            Q20=makeQuery(id+"F2.imprint","IMPRINT",FACE,{"disambiguationData":[TD([[makeQuery(id+"F2.imprint","IMPRINT",EDGE,{"derivedFrom":sQuery(id+"F2.wireOp",EDGE,"E35.6.0.8")}),1.0]])]});
            var Q21;
            Q21=makeQuery(id+"F2.imprint","IMPRINT",FACE,{"disambiguationData":[TD([[makeQuery(id+"F2.imprint","IMPRINT",EDGE,{"derivedFrom":sQuery(id+"F2.wireOp",EDGE,"E35.7.0.4")}),-1.0]])]});
            var Q22;
            Q22=makeQuery(id+"F2.imprint","IMPRINT",FACE,{"disambiguationData":[TD([[makeQuery(id+"F2.imprint","IMPRINT",EDGE,{"derivedFrom":sQuery(id+"F2.wireOp",EDGE,"E35.7.0.0")}),1.0]])]});
            var Q23;
            Q23=makeQuery(id+"F2.imprint","IMPRINT",FACE,{"disambiguationData":[TD([[makeQuery(id+"F2.imprint","IMPRINT",EDGE,{"derivedFrom":sQuery(id+"F2.wireOp",EDGE,"E35.7.0.8")}),1.0]])]});
            var Q24;
            Q24=makeQuery(id+"F2.imprint","IMPRINT",FACE,{"disambiguationData":[TD([[makeQuery(id+"F2.imprint","IMPRINT",EDGE,{"derivedFrom":sQuery(id+"F2.wireOp",EDGE,"E35.8.0.4")}),-1.0]])]});
            var Q25;
            Q25=makeQuery(id+"F2.imprint","IMPRINT",FACE,{"disambiguationData":[TD([[makeQuery(id+"F2.imprint","IMPRINT",EDGE,{"derivedFrom":sQuery(id+"F2.wireOp",EDGE,"E35.8.0.0")}),1.0]])]});
            var Q26;
            Q26=makeQuery(id+"F2.imprint","IMPRINT",FACE,{"disambiguationData":[TD([[makeQuery(id+"F2.imprint","IMPRINT",EDGE,{"derivedFrom":sQuery(id+"F2.wireOp",EDGE,"E35.8.0.8")}),1.0]])]});
            var Q27;
            Q27=makeQuery(id+"F2.imprint","IMPRINT",FACE,{"disambiguationData":[TD([[makeQuery(id+"F2.imprint","IMPRINT",EDGE,{"derivedFrom":sQuery(id+"F2.wireOp",EDGE,"E35.9.0.0")}),1.0]])]});
            var Q28;
            Q28=makeQuery(id+"F2.imprint","IMPRINT",FACE,{"disambiguationData":[TD([[makeQuery(id+"F2.imprint","IMPRINT",EDGE,{"derivedFrom":sQuery(id+"F2.wireOp",EDGE,"E35.9.0.4")}),-1.0]])]});
            var Q29;
            Q29=makeQuery(id+"F2.imprint","IMPRINT",FACE,{"disambiguationData":[TD([[makeQuery(id+"F2.imprint","IMPRINT",EDGE,{"derivedFrom":sQuery(id+"F2.wireOp",EDGE,"E35.9.0.8")}),1.0]])]});
            var Q30;
            Q30=makeQuery(id+"F2.imprint","IMPRINT",FACE,{"disambiguationData":[TD([[makeQuery(id+"F2.imprint","IMPRINT",EDGE,{"derivedFrom":sQuery(id+"F2.wireOp",EDGE,"E36.0.10.0")}),1.0]])]});
            var Q31;
            Q31=makeQuery(id+"F2.imprint","IMPRINT",FACE,{"disambiguationData":[TD([[makeQuery(id+"F2.imprint","IMPRINT",EDGE,{"derivedFrom":sQuery(id+"F2.wireOp",EDGE,"E36.12.10.0")}),-1.0]])]});
            var Q32;
            Q32=makeQuery(id+"F2.imprint","IMPRINT",FACE,{"disambiguationData":[TD([[makeQuery(id+"F2.imprint","IMPRINT",EDGE,{"derivedFrom":sQuery(id+"F2.wireOp",EDGE,"E36.24.10.0")}),1.0]])]});
            var Q33;
            Q33=makeQuery(id+"F2.imprint","IMPRINT",FACE,{"disambiguationData":[TD([[makeQuery(id+"F2.imprint","IMPRINT",EDGE,{"derivedFrom":sQuery(id+"F2.wireOp",EDGE,"E36.12.11.0")}),-1.0]])]});
            var Q34;
            Q34=makeQuery(id+"F2.imprint","IMPRINT",FACE,{"disambiguationData":[TD([[makeQuery(id+"F2.imprint","IMPRINT",EDGE,{"derivedFrom":sQuery(id+"F2.wireOp",EDGE,"E36.0.11.0")}),1.0]])]});
            var Q35;
            Q35=makeQuery(id+"F2.imprint","IMPRINT",FACE,{"disambiguationData":[TD([[makeQuery(id+"F2.imprint","IMPRINT",EDGE,{"derivedFrom":sQuery(id+"F2.wireOp",EDGE,"E37.bottom")}),-1.0]])]});
            var Q36;
            Q36=makeQuery(id+"F2.imprint","IMPRINT",FACE,{"disambiguationData":[TD([[makeQuery(id+"F2.imprint","IMPRINT",EDGE,{"derivedFrom":sQuery(id+"F2.wireOp",EDGE,"E36.24.11.0")}),1.0]])]});
            var Q37;
            Q37=makeQuery(id+"F2.imprint","IMPRINT",FACE,{"disambiguationData":[TD([[makeQuery(id+"F2.imprint","IMPRINT",EDGE,{"derivedFrom":sQuery(id+"F2.wireOp",EDGE,"E38.top")}),-1.0]])]});
            extrude(context, id + "F5", {"entities" : qUnion([Q0, Q1, Q2, Q3, Q4, Q5, Q6, Q7, Q8, Q9, Q10, Q11, Q12, Q13, Q14, Q15, Q16, Q17, Q18, Q19, Q20, Q21, Q22, Q23, Q24, Q25, Q26, Q27, Q28, Q29, Q30, Q31, Q32, Q33, Q34, Q35, Q36, Q37]), "operationType" : NewBodyOperationType.REMOVE, "endBound" : BoundingType.THROUGH_ALL, "oppositeDirection" : true, "depth" : 25 * mm});
        }
    });
